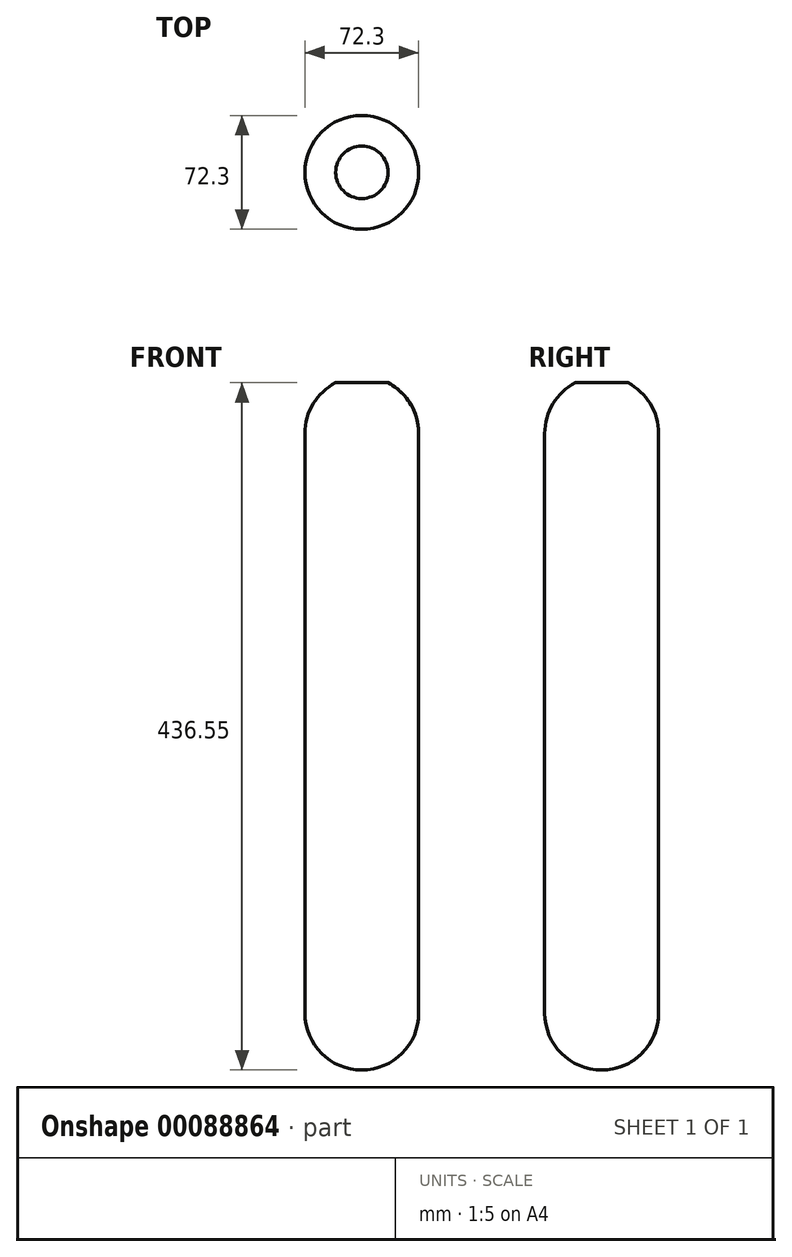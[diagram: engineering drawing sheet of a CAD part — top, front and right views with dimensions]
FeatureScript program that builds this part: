
annotation { "Feature Type Name" : "Feature", "Feature Type Description" : "" }
export const myFeature = defineFeature(function(context is Context, id is Id, definition is map)
    precondition{}
    {
        {
            var Q0;
            Q0=qCreatedBy(makeId("Right.planeOp"),FACE);
            var sketch = newSketch(context, id + "F0", { "sketchPlane" : qUnion([Q0])});
            skLineSegment(sketch, "E0", {"start": v(29.8, 0) * mm, "end": v(29.8, 184.15) * mm});
            skArc(sketch, "E1", {"start": v(29.8, 184.15) * mm, "mid": v(25.83, 199) * mm, "end": v(15, 209.9) * mm});
            skLineSegment(sketch, "E2", {"start": v(15, 209.9) * mm, "end": v(0, 209.9) * mm});
            skLineSegment(sketch, "E3", {"start": v(0, 209.9) * mm, "end": v(0, 216.25) * mm});
            skLineSegment(sketch, "E4", {"start": v(29.8, 0) * mm, "end": v(29.8, -184.15) * mm});
            skArc(sketch, "E5", {"start": v(29.8, -184.15) * mm, "mid": v(21.07, -205.22) * mm, "end": v(0, -213.95) * mm});
            skLineSegment(sketch, "E6", {"start": v(0, -213.95) * mm, "end": v(0, -220.3) * mm});
            skArc(sketch, "E7.0", {"start": v(36.15, -184.15) * mm, "mid": v(25.56, -209.7) * mm, "end": v(0, -220.3) * mm});
            skLineSegment(sketch, "E7.1", {"start": v(16.62, 216.25) * mm, "end": v(-12.6, 216.25) * mm});
            skArc(sketch, "E7.2", {"start": v(36.15, 184.15) * mm, "mid": v(30.88, 202.94) * mm, "end": v(16.62, 216.25) * mm});
            skLineSegment(sketch, "E7.3", {"start": v(36.15, 0) * mm, "end": v(36.15, 184.15) * mm});
            skLineSegment(sketch, "E7.4", {"start": v(36.15, 0) * mm, "end": v(36.15, -184.15) * mm});
            skLineSegment(sketch, "E8", {"start": v(0, 224.02) * mm, "end": v(0, -228.4) * mm});
            skSolve(sketch);
        }
        {
            var Q0;
            Q0 = qSketchRegion(id + "F0", true);
            var Q1;
            Q1=sQuery(id+"F0.wireOp",EDGE,"E8");
            revolve(context, id + "F1", {"entities" : qUnion([Q0]), "axis" : qUnion([Q1]), "revolveType" : RevolveType.FULL});
        }
    });
